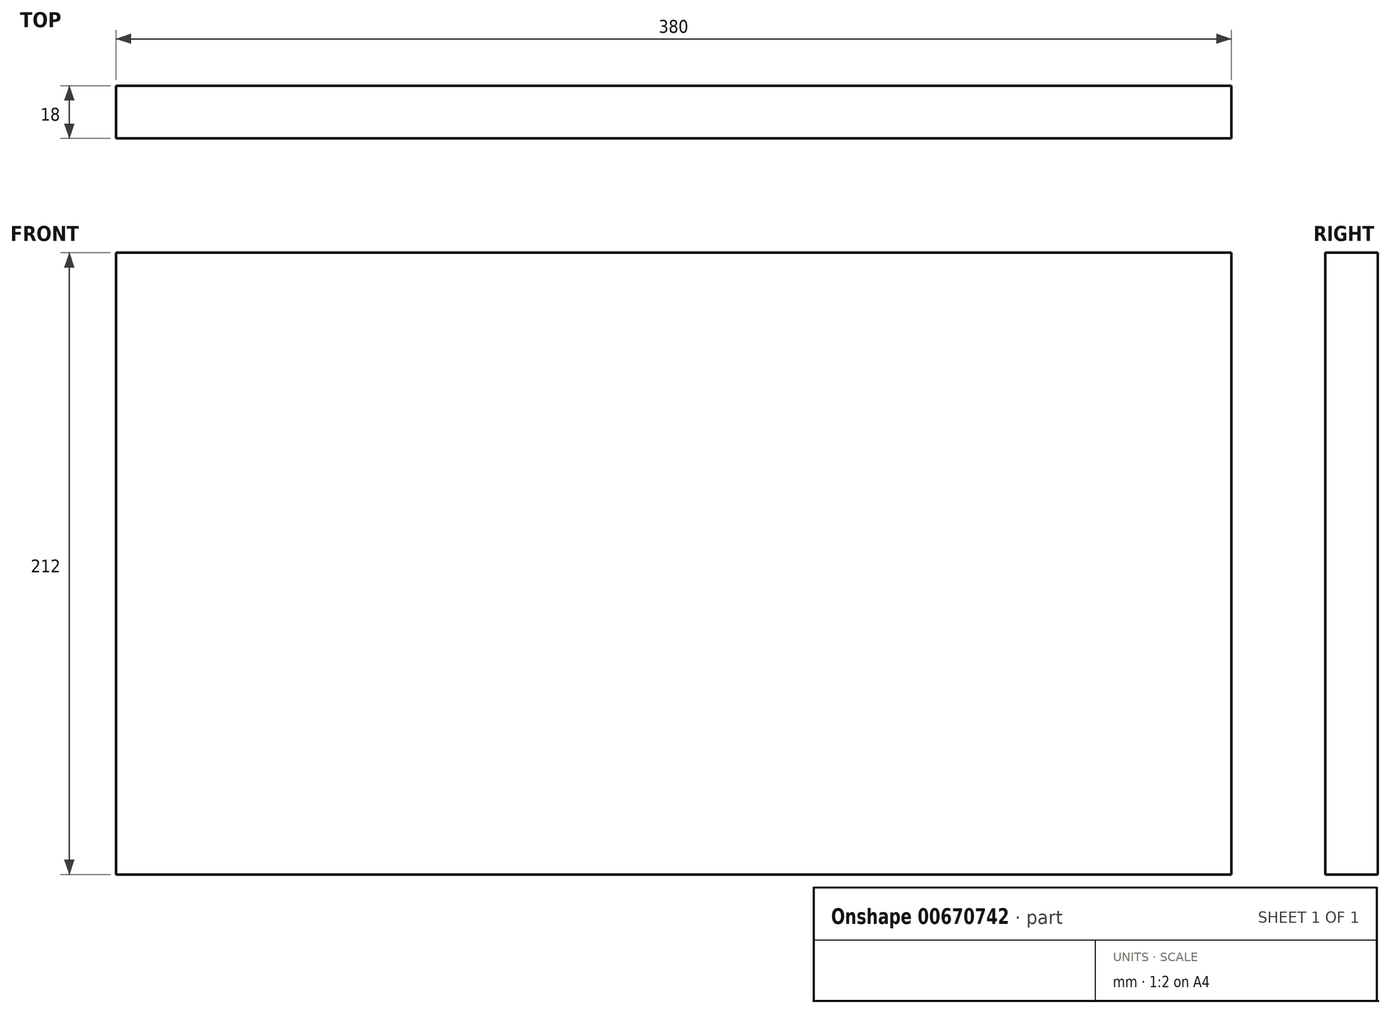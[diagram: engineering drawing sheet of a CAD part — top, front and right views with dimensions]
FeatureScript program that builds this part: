
annotation { "Feature Type Name" : "Feature", "Feature Type Description" : "" }
export const myFeature = defineFeature(function(context is Context, id is Id, definition is map)
    precondition{}
    {
        {
            var Q0;
            Q0=qCreatedBy(makeId("Front.planeOp"),FACE);
            var sketch = newSketch(context, id + "F0", { "sketchPlane" : qUnion([Q0])});
            skLineSegment(sketch, "E0.bottom", {"start": v(190, 106) * mm, "end": v(-190, 106) * mm});
            skLineSegment(sketch, "E0.top", {"start": v(190, -106) * mm, "end": v(-190, -106) * mm});
            skLineSegment(sketch, "E0.left", {"start": v(190, 106) * mm, "end": v(190, -106) * mm});
            skLineSegment(sketch, "E0.right", {"start": v(-190, 106) * mm, "end": v(-190, -106) * mm});
            skPoint(sketch, "E0.middle", {"position": v(0, 0) * mm});
            skSolve(sketch);
        }
        {
            var Q0;
            Q0 = qSketchRegion(id + "F0", true);
            extrude(context, id + "F1", {"entities" : qUnion([Q0]), "endBound" : BoundingType.SYMMETRIC, "depth" : 18 * mm, "offsetDistance" : 25 * mm});
        }
    });
